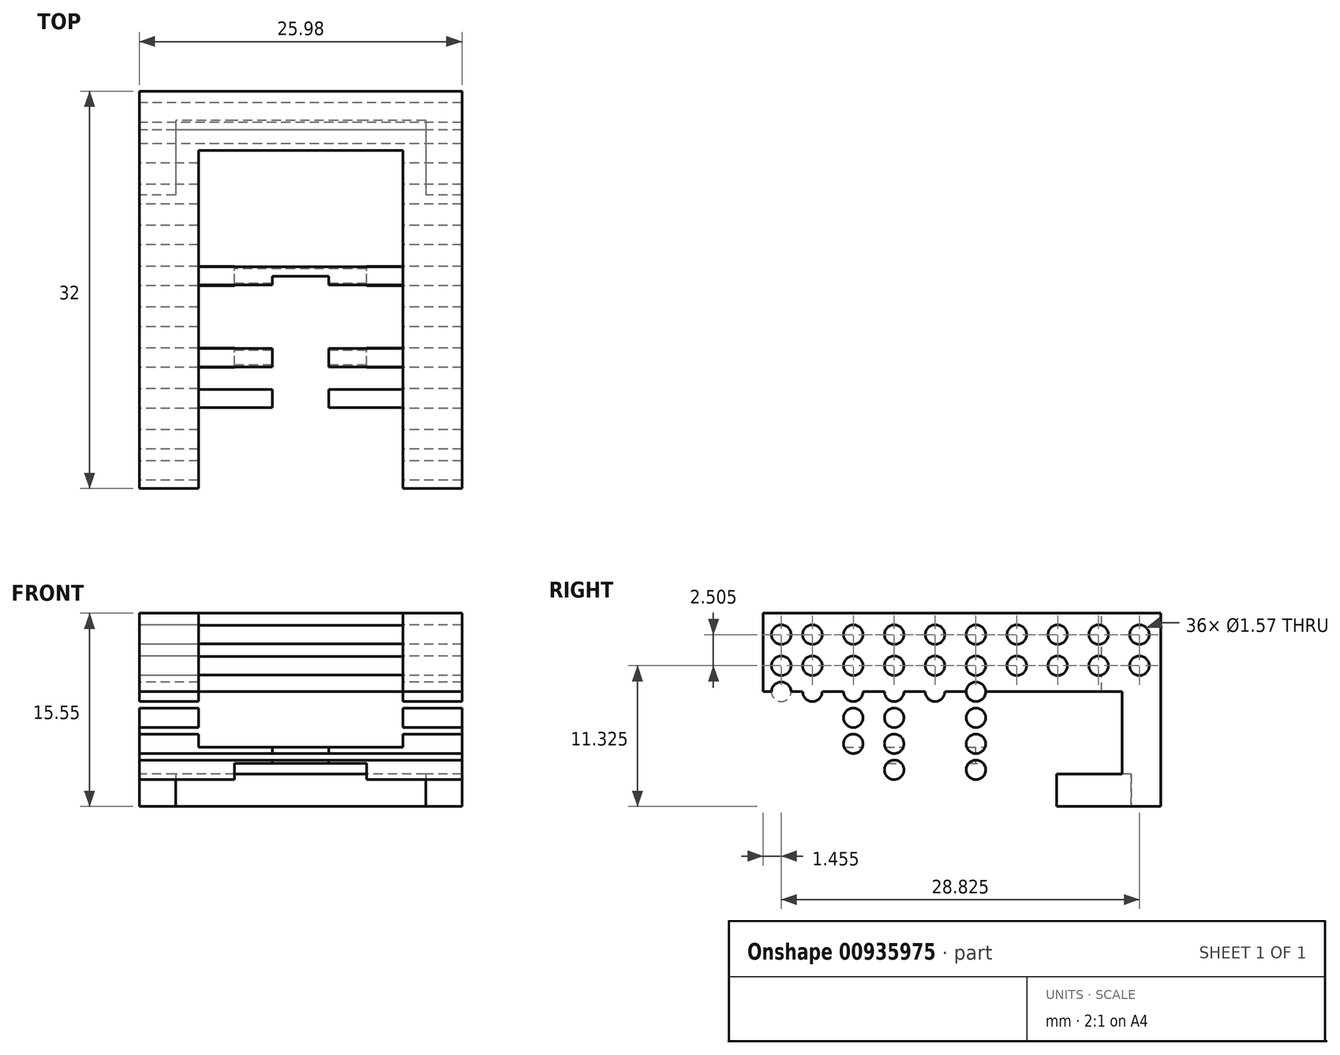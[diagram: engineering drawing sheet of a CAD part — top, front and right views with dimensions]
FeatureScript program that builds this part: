
annotation { "Feature Type Name" : "Feature", "Feature Type Description" : "" }
export const myFeature = defineFeature(function(context is Context, id is Id, definition is map)
    precondition{}
    {
        {
            var Q0;
            Q0=qCreatedBy(makeId("Front.planeOp"),FACE);
            var sketch = newSketch(context, id + "F0", { "sketchPlane" : qUnion([Q0])});
            skLineSegment(sketch, "E0.bottom", {"start": v(8.22, 0) * mm, "end": v(-8.23, 0) * mm});
            skLineSegment(sketch, "E0.top", {"start": v(8.23, 15.55) * mm, "end": v(-8.22, 15.55) * mm});
            skLineSegment(sketch, "E0.left", {"start": v(8.22, 0) * mm, "end": v(8.23, 15.55) * mm});
            skLineSegment(sketch, "E0.right", {"start": v(-8.23, 0) * mm, "end": v(-8.22, 15.55) * mm});
            skPoint(sketch, "E0.middle", {"position": v(0, 7.78) * mm});
            skLineSegment(sketch, "E1.bottom", {"start": v(8.23, 15.55) * mm, "end": v(12.99, 15.55) * mm});
            skLineSegment(sketch, "E1.top", {"start": v(8.23, 0) * mm, "end": v(12.98, 0) * mm});
            skLineSegment(sketch, "E1.left", {"start": v(8.23, 15.55) * mm, "end": v(8.23, 0) * mm});
            skLineSegment(sketch, "E1.right", {"start": v(12.99, 15.55) * mm, "end": v(12.98, 0) * mm});
            skLineSegment(sketch, "E2.bottom", {"start": v(-8.23, 0) * mm, "end": v(-12.98, 0) * mm});
            skLineSegment(sketch, "E2.top", {"start": v(-8.23, 15.55) * mm, "end": v(-12.98, 15.55) * mm});
            skLineSegment(sketch, "E2.left", {"start": v(-8.23, 0) * mm, "end": v(-8.23, 15.55) * mm});
            skLineSegment(sketch, "E2.right", {"start": v(-12.98, 0) * mm, "end": v(-12.98, 15.55) * mm});
            skSolve(sketch);
        }
        {
            var Q0;
            Q0=makeQuery(id+"F0.imprint","IMPRINT",FACE,{"disambiguationData":[TD([[makeQuery(id+"F0.imprint","IMPRINT",EDGE,{"derivedFrom":sQuery(id+"F0.wireOp",EDGE,"E2.bottom")}),-1.0]])]});
            var Q1;
            Q1=makeQuery(id+"F0.imprint","IMPRINT",FACE,{"disambiguationData":[TD([[makeQuery(id+"F0.imprint","IMPRINT",EDGE,{"derivedFrom":sQuery(id+"F0.wireOp",EDGE,"E1.bottom")}),-1.0]])]});
            extrude(context, id + "F1", {"entities" : qUnion([Q0, Q1]), "depth" : 32 * mm, "offsetDistance" : 25 * mm});
        }
        {
            var Q0;
            Q0=makeQuery(id+"F0.imprint","IMPRINT",FACE,{"disambiguationData":[TD([[makeQuery(id+"F0.imprint","IMPRINT",EDGE,{"derivedFrom":sQuery(id+"F0.wireOp",EDGE,"E0.bottom")}),-1.0]])]});
            extrude(context, id + "F2", {"entities" : qUnion([Q0]), "operationType" : NewBodyOperationType.ADD, "depth" : 4.76 * mm, "offsetDistance" : 25 * mm});
        }
        {
            var Q0;
            Q0=makeQuery(id+"F2.opExtrude","CAP_FACE",FACE,{"disambiguationData":[OSD([sQuery(id+"F0.wireOp",EDGE,"E0.bottom"),sQuery(id+"F0.wireOp",EDGE,"E0.top"),sQuery(id+"F0.wireOp",EDGE,"E1.left"),sQuery(id+"F0.wireOp",EDGE,"E2.left")])],"isStart":false});
            var sketch = newSketch(context, id + "F3", { "sketchPlane" : qUnion([Q0])});
            skLineSegment(sketch, "E3.bottom", {"start": v(-8.23, 0) * mm, "end": v(8.23, 0) * mm});
            skLineSegment(sketch, "E3.top", {"start": v(-8.23, 4.76) * mm, "end": v(8.23, 4.76) * mm});
            skLineSegment(sketch, "E3.left", {"start": v(-8.23, 0) * mm, "end": v(-8.23, 4.76) * mm});
            skLineSegment(sketch, "E3.right", {"start": v(8.23, 0) * mm, "end": v(8.23, 4.76) * mm});
            skLineSegment(sketch, "E4.bottom", {"start": v(-5.32, 3.46) * mm, "end": v(5.32, 3.46) * mm});
            skLineSegment(sketch, "E4.top", {"start": v(-5.32, 0) * mm, "end": v(5.32, 0) * mm});
            skLineSegment(sketch, "E4.left", {"start": v(-5.32, 3.46) * mm, "end": v(-5.32, 0) * mm});
            skLineSegment(sketch, "E4.right", {"start": v(5.32, 3.46) * mm, "end": v(5.32, 0) * mm});
            skSolve(sketch);
        }
        {
            var Q0;
            Q0=makeQuery(id+"F3.imprint","IMPRINT",FACE,{"disambiguationData":[TD([[makeQuery(id+"F3.imprint","IMPRINT",EDGE,{"derivedFrom":sQuery(id+"F3.wireOp",EDGE,"E3.top")}),-1.0]])]});
            extrude(context, id + "F4", {"entities" : qUnion([Q0]), "operationType" : NewBodyOperationType.ADD, "depth" : 27.24 * mm, "offsetDistance" : 25 * mm});
        }
        {
            var Q0;
            Q0=makeQuery(id+"F1.opExtrude","SWEPT_FACE",FACE,{"disambiguationData":[OSD([sQuery(id+"F0.wireOp",EDGE,"E2.right")])]});
            var sketch = newSketch(context, id + "F5", { "sketchPlane" : qUnion([Q0])});
            skLineSegment(sketch, "E5.bottom", {"start": v(0, 0) * mm, "end": v(4.76, 0) * mm});
            skLineSegment(sketch, "E5.top", {"start": v(0, -5) * mm, "end": v(4.76, -5) * mm});
            skLineSegment(sketch, "E5.left", {"start": v(0, 0) * mm, "end": v(0, -5) * mm});
            skLineSegment(sketch, "E5.right", {"start": v(4.76, 0) * mm, "end": v(4.76, -5) * mm});
            skLineSegment(sketch, "E6", {"start": v(0, 1.39) * mm, "end": v(8.37, 1.39) * mm});
            skLineSegment(sketch, "E7.bottom", {"start": v(8.37, 0) * mm, "end": v(12.6, 0) * mm});
            skLineSegment(sketch, "E7.top", {"start": v(8.37, 9.23) * mm, "end": v(12.6, 9.23) * mm});
            skLineSegment(sketch, "E7.left", {"start": v(8.37, 0) * mm, "end": v(8.37, 9.23) * mm});
            skLineSegment(sketch, "E7.right", {"start": v(12.6, 0) * mm, "end": v(12.6, 9.23) * mm});
            skLineSegment(sketch, "E8.bottom", {"start": v(8.37, 9.23) * mm, "end": v(3.12, 9.23) * mm});
            skLineSegment(sketch, "E8.top", {"start": v(8.37, 2.6) * mm, "end": v(3.12, 2.6) * mm});
            skLineSegment(sketch, "E8.left", {"start": v(8.37, 9.23) * mm, "end": v(8.37, 2.6) * mm});
            skLineSegment(sketch, "E8.right", {"start": v(3.12, 9.23) * mm, "end": v(3.12, 2.6) * mm});
            skLineSegment(sketch, "E9.bottom", {"start": v(-4.28, 0) * mm, "end": v(-0.52, 0) * mm});
            skLineSegment(sketch, "E9.top", {"start": v(-4.28, 2.6) * mm, "end": v(-0.52, 2.6) * mm});
            skLineSegment(sketch, "E9.left", {"start": v(-4.28, 0) * mm, "end": v(-4.28, 2.6) * mm});
            skLineSegment(sketch, "E9.right", {"start": v(-0.52, 0) * mm, "end": v(-0.52, 2.6) * mm});
            skSolve(sketch);
        }
        {
            var Q0;
            Q0=makeQuery(id+"F5.imprint","IMPRINT",FACE,{"disambiguationData":[TD([[makeQuery(id+"F5.imprint","IMPRINT",EDGE,{"derivedFrom":sQuery(id+"F5.wireOp",EDGE,"E8.bottom")}),1.0]])]});
            var Q1;
            {var subQ3=sQuery(id+"F5.wireOp",EDGE,"E7.bottom");Q1=makeQuery(id+"F5.imprint","IMPRINT",FACE,{"disambiguationData":[TD([[makeQuery(id+"F5.imprint","IMPRINT",EDGE,{"derivedFrom":subQ3}),-1.0]])]});}
            extrude(context, id + "F6", {"entities" : qUnion([Q0, Q1]), "operationType" : NewBodyOperationType.REMOVE, "oppositeDirection" : true, "depth" : 25.98 * mm, "offsetDistance" : 25 * mm});
        }
        {
            var Q0;
            Q0=makeQuery(id+"F4.opExtrude","SWEPT_FACE",FACE,{"disambiguationData":[OSD([sQuery(id+"F3.wireOp",EDGE,"E3.top")])]});
            var sketch = newSketch(context, id + "F7", { "sketchPlane" : qUnion([Q0])});
            skLineSegment(sketch, "E10.bottom", {"start": v(2.27, -29.7) * mm, "end": v(-2.28, -29.7) * mm});
            skLineSegment(sketch, "E10.top", {"start": v(2.28, -14.9) * mm, "end": v(-2.27, -14.9) * mm});
            skLineSegment(sketch, "E10.left", {"start": v(2.27, -29.7) * mm, "end": v(2.28, -14.9) * mm});
            skLineSegment(sketch, "E10.right", {"start": v(-2.28, -29.7) * mm, "end": v(-2.27, -14.9) * mm});
            skPoint(sketch, "E10.middle", {"position": v(0, -22.3) * mm});
            skPoint(sketch, "E10.middle.positionSnap0", {"position": v(0, -32) * mm});
            skPoint(sketch, "E10.middle.positionSnap1", {"position": v(-8.23, -22.3) * mm});
            skPoint(sketch, "E10.centerSnap0", {"position": v(0, -32) * mm});
            skPoint(sketch, "E10.centerSnap1", {"position": v(-8.23, -22.3) * mm});
            skSolve(sketch);
        }
        {
            var Q0;
            Q0=makeQuery(id+"F7.imprint","IMPRINT",FACE,{"disambiguationData":[TD([[makeQuery(id+"F7.imprint","IMPRINT",EDGE,{"derivedFrom":sQuery(id+"F7.wireOp",EDGE,"E10.bottom")}),-1.0]])]});
            extrude(context, id + "F8", {"entities" : qUnion([Q0]), "operationType" : NewBodyOperationType.REMOVE, "oppositeDirection" : true, "depth" : 2 * mm, "offsetDistance" : 25 * mm});
        }
        {
            var Q0;
            Q0=makeQuery(id+"F1.opExtrude","SWEPT_FACE",FACE,{"disambiguationData":[OSD([sQuery(id+"F0.wireOp",EDGE,"E2.right")])]});
            var sketch = newSketch(context, id + "F9", { "sketchPlane" : qUnion([Q0])});
            skLineSegment(sketch, "E11.bottom", {"start": v(32, 15.55) * mm, "end": v(0, 15.55) * mm});
            skLineSegment(sketch, "E11.top", {"start": v(32, 9.23) * mm, "end": v(0, 9.23) * mm});
            skLineSegment(sketch, "E11.left", {"start": v(32, 15.55) * mm, "end": v(32, 9.23) * mm});
            skLineSegment(sketch, "E11.right", {"start": v(0, 15.55) * mm, "end": v(0, 9.23) * mm});
            skLineSegment(sketch, "E12.bottom", {"start": v(32, 0) * mm, "end": v(37.47, 0) * mm});
            skLineSegment(sketch, "E12.top", {"start": v(32, 4.76) * mm, "end": v(37.47, 4.76) * mm});
            skLineSegment(sketch, "E12.left", {"start": v(32, 0) * mm, "end": v(32, 4.76) * mm});
            skLineSegment(sketch, "E12.right", {"start": v(37.47, 0) * mm, "end": v(37.47, 4.76) * mm});
            skLineSegment(sketch, "E13.bottom", {"start": v(12.6, 9.23) * mm, "end": v(32, 9.23) * mm});
            skLineSegment(sketch, "E13.left", {"start": v(12.6, 9.23) * mm, "end": v(12.6, 4.76) * mm});
            skLineSegment(sketch, "E13.right", {"start": v(32, 9.23) * mm, "end": v(32, 4.76) * mm});
            skLineSegment(sketch, "E14.bottom", {"start": v(-1.17, 15.55) * mm, "end": v(32.9, 15.55) * mm});
            skLineSegment(sketch, "E14.top", {"start": v(-1.17, 13.83) * mm, "end": v(32.9, 13.83) * mm});
            skLineSegment(sketch, "E14.left", {"start": v(-1.17, 15.55) * mm, "end": v(-1.17, 13.83) * mm});
            skLineSegment(sketch, "E14.right", {"start": v(32.9, 15.55) * mm, "end": v(32.9, 13.83) * mm});
            skLineSegment(sketch, "E15.bottom", {"start": v(0, 9.23) * mm, "end": v(1.72, 9.23) * mm});
            skLineSegment(sketch, "E15.top", {"start": v(0, 16.76) * mm, "end": v(1.72, 16.76) * mm});
            skLineSegment(sketch, "E15.left", {"start": v(0, 9.23) * mm, "end": v(0, 16.76) * mm});
            skLineSegment(sketch, "E15.right", {"start": v(1.72, 9.23) * mm, "end": v(1.72, 16.76) * mm});
            skCircle(sketch, "E16", {"center": v(1.72, 13.83) * mm, "radius": 0.79 * mm});
            skLineSegment(sketch, "E17.bottom", {"start": v(2.5, 9.23) * mm, "end": v(4.22, 9.23) * mm});
            skLineSegment(sketch, "E17.top", {"start": v(2.5, 16.72) * mm, "end": v(4.22, 16.72) * mm});
            skLineSegment(sketch, "E17.left", {"start": v(2.5, 9.23) * mm, "end": v(2.5, 16.72) * mm});
            skLineSegment(sketch, "E17.right", {"start": v(4.22, 9.23) * mm, "end": v(4.22, 16.72) * mm});
            skCircle(sketch, "E18", {"center": v(5, 13.83) * mm, "radius": 0.79 * mm});
            skLineSegment(sketch, "E19.bottom", {"start": v(5.8, 9.23) * mm, "end": v(7.51, 9.23) * mm});
            skLineSegment(sketch, "E19.top", {"start": v(5.8, 16.72) * mm, "end": v(7.51, 16.72) * mm});
            skLineSegment(sketch, "E19.left", {"start": v(5.8, 9.23) * mm, "end": v(5.8, 16.72) * mm});
            skLineSegment(sketch, "E19.right", {"start": v(7.51, 9.23) * mm, "end": v(7.51, 16.72) * mm});
            skCircle(sketch, "E20", {"center": v(8.3, 13.83) * mm, "radius": 0.79 * mm});
            skLineSegment(sketch, "E21.bottom", {"start": v(9.08, 9.23) * mm, "end": v(10.8, 9.23) * mm});
            skLineSegment(sketch, "E21.top", {"start": v(9.08, 16.72) * mm, "end": v(10.8, 16.72) * mm});
            skLineSegment(sketch, "E21.left", {"start": v(9.08, 9.23) * mm, "end": v(9.08, 16.72) * mm});
            skLineSegment(sketch, "E21.right", {"start": v(10.8, 9.23) * mm, "end": v(10.8, 16.72) * mm});
            skCircle(sketch, "E22", {"center": v(11.59, 13.83) * mm, "radius": 0.79 * mm});
            skLineSegment(sketch, "E23.bottom", {"start": v(12.37, 9.23) * mm, "end": v(14.1, 9.23) * mm});
            skLineSegment(sketch, "E23.top", {"start": v(12.37, 16.72) * mm, "end": v(14.1, 16.72) * mm});
            skLineSegment(sketch, "E23.left", {"start": v(12.37, 9.23) * mm, "end": v(12.37, 16.72) * mm});
            skLineSegment(sketch, "E23.right", {"start": v(14.1, 9.23) * mm, "end": v(14.1, 16.72) * mm});
            skCircle(sketch, "E24", {"center": v(14.88, 13.83) * mm, "radius": 0.79 * mm});
            skLineSegment(sketch, "E25.bottom", {"start": v(15.66, 9.23) * mm, "end": v(17.38, 9.23) * mm});
            skLineSegment(sketch, "E25.top", {"start": v(15.66, 16.72) * mm, "end": v(17.38, 16.72) * mm});
            skLineSegment(sketch, "E25.left", {"start": v(15.66, 9.23) * mm, "end": v(15.66, 16.72) * mm});
            skLineSegment(sketch, "E25.right", {"start": v(17.38, 9.23) * mm, "end": v(17.38, 16.72) * mm});
            skCircle(sketch, "E26", {"center": v(18.17, 13.83) * mm, "radius": 0.79 * mm});
            skLineSegment(sketch, "E27.bottom", {"start": v(18.95, 9.23) * mm, "end": v(20.67, 9.23) * mm});
            skLineSegment(sketch, "E27.top", {"start": v(18.95, 16.72) * mm, "end": v(20.67, 16.72) * mm});
            skLineSegment(sketch, "E27.left", {"start": v(18.95, 9.23) * mm, "end": v(18.95, 16.72) * mm});
            skLineSegment(sketch, "E27.right", {"start": v(20.67, 9.23) * mm, "end": v(20.67, 16.72) * mm});
            skCircle(sketch, "E28", {"center": v(21.46, 13.83) * mm, "radius": 0.79 * mm});
            skLineSegment(sketch, "E29.bottom", {"start": v(22.24, 9.23) * mm, "end": v(23.96, 9.23) * mm});
            skLineSegment(sketch, "E29.top", {"start": v(22.24, 16.72) * mm, "end": v(23.96, 16.72) * mm});
            skLineSegment(sketch, "E29.left", {"start": v(22.24, 9.23) * mm, "end": v(22.24, 16.72) * mm});
            skLineSegment(sketch, "E29.right", {"start": v(23.96, 9.23) * mm, "end": v(23.96, 16.72) * mm});
            skCircle(sketch, "E30", {"center": v(24.75, 13.83) * mm, "radius": 0.79 * mm});
            skLineSegment(sketch, "E31.bottom", {"start": v(25.53, 9.23) * mm, "end": v(27.25, 9.23) * mm});
            skLineSegment(sketch, "E31.top", {"start": v(25.53, 16.72) * mm, "end": v(27.25, 16.72) * mm});
            skLineSegment(sketch, "E31.left", {"start": v(25.53, 9.23) * mm, "end": v(25.53, 16.72) * mm});
            skLineSegment(sketch, "E31.right", {"start": v(27.25, 9.23) * mm, "end": v(27.25, 16.72) * mm});
            skCircle(sketch, "E32", {"center": v(28.04, 13.83) * mm, "radius": 0.79 * mm});
            skLineSegment(sketch, "E33.bottom", {"start": v(28.82, 9.23) * mm, "end": v(30.54, 9.23) * mm});
            skLineSegment(sketch, "E33.top", {"start": v(28.82, 16.72) * mm, "end": v(30.54, 16.72) * mm});
            skLineSegment(sketch, "E33.left", {"start": v(28.82, 9.23) * mm, "end": v(28.82, 16.72) * mm});
            skLineSegment(sketch, "E33.right", {"start": v(30.54, 9.23) * mm, "end": v(30.54, 16.72) * mm});
            skLineSegment(sketch, "E34.bottom", {"start": v(-1.17, 13.04) * mm, "end": v(32.9, 13.04) * mm});
            skLineSegment(sketch, "E34.top", {"start": v(-1.17, 11.32) * mm, "end": v(32.9, 11.32) * mm});
            skLineSegment(sketch, "E34.left", {"start": v(-1.17, 13.04) * mm, "end": v(-1.17, 11.32) * mm});
            skLineSegment(sketch, "E34.right", {"start": v(32.9, 13.04) * mm, "end": v(32.9, 11.32) * mm});
            skCircle(sketch, "E35", {"center": v(1.72, 11.32) * mm, "radius": 0.79 * mm});
            skCircle(sketch, "E36", {"center": v(5, 11.32) * mm, "radius": 0.79 * mm});
            skCircle(sketch, "E37", {"center": v(8.3, 11.32) * mm, "radius": 0.79 * mm});
            skCircle(sketch, "E38", {"center": v(11.59, 11.32) * mm, "radius": 0.79 * mm});
            skCircle(sketch, "E39", {"center": v(14.88, 11.32) * mm, "radius": 0.79 * mm});
            skCircle(sketch, "E40", {"center": v(18.17, 11.32) * mm, "radius": 0.79 * mm});
            skCircle(sketch, "E41", {"center": v(21.46, 11.32) * mm, "radius": 0.79 * mm});
            skCircle(sketch, "E42", {"center": v(24.75, 11.32) * mm, "radius": 0.79 * mm});
            skCircle(sketch, "E43", {"center": v(28.04, 11.32) * mm, "radius": 0.79 * mm});
            skCircle(sketch, "E44", {"center": v(30.54, 13.83) * mm, "radius": 0.79 * mm});
            skCircle(sketch, "E45", {"center": v(30.54, 11.32) * mm, "radius": 0.79 * mm});
            skPoint(sketch, "E46.firstSnap0", {"position": v(12.6, 7.13) * mm});
            skLineSegment(sketch, "E46.bottom", {"start": v(11.82, 7.13) * mm, "end": v(32.9, 7.13) * mm});
            skLineSegment(sketch, "E46.top", {"start": v(11.82, 5.04) * mm, "end": v(32.9, 5.04) * mm});
            skLineSegment(sketch, "E46.left", {"start": v(11.82, 7.13) * mm, "end": v(11.82, 5.04) * mm});
            skLineSegment(sketch, "E46.right", {"start": v(32.9, 7.13) * mm, "end": v(32.9, 5.04) * mm});
            skCircle(sketch, "E47", {"center": v(14.88, 7.13) * mm, "radius": 0.79 * mm});
            skCircle(sketch, "E48", {"center": v(18.17, 7.13) * mm, "radius": 0.79 * mm});
            skCircle(sketch, "E49", {"center": v(21.46, 7.13) * mm, "radius": 0.79 * mm});
            skCircle(sketch, "E50", {"center": v(24.75, 7.13) * mm, "radius": 0.79 * mm});
            skCircle(sketch, "E51", {"center": v(28.04, 7.13) * mm, "radius": 0.79 * mm});
            skCircle(sketch, "E52", {"center": v(30.54, 7.13) * mm, "radius": 0.79 * mm});
            skCircle(sketch, "E53", {"center": v(14.88, 9.23) * mm, "radius": 0.79 * mm});
            skCircle(sketch, "E54", {"center": v(18.17, 9.23) * mm, "radius": 0.79 * mm});
            skCircle(sketch, "E55", {"center": v(21.46, 9.23) * mm, "radius": 0.79 * mm});
            skCircle(sketch, "E56", {"center": v(24.75, 9.23) * mm, "radius": 0.79 * mm});
            skCircle(sketch, "E57", {"center": v(28.04, 9.23) * mm, "radius": 0.79 * mm});
            skCircle(sketch, "E58", {"center": v(30.54, 9.23) * mm, "radius": 0.79 * mm});
            skLineSegment(sketch, "E59", {"start": v(41.5, -2.03) * mm, "end": v(41.5, -4.13) * mm});
            skLineSegment(sketch, "E60.bottom", {"start": v(11.82, -2.6) * mm, "end": v(32.9, -2.6) * mm});
            skLineSegment(sketch, "E60.top", {"start": v(11.82, -4.69) * mm, "end": v(32.9, -4.69) * mm});
            skLineSegment(sketch, "E60.left", {"start": v(11.82, -2.6) * mm, "end": v(11.82, -4.69) * mm});
            skLineSegment(sketch, "E60.right", {"start": v(32.9, -2.6) * mm, "end": v(32.9, -4.69) * mm});
            skLineSegment(sketch, "E61.top", {"start": v(11.82, 2.94) * mm, "end": v(32.9, 2.94) * mm});
            skLineSegment(sketch, "E61.left", {"start": v(11.82, 5.04) * mm, "end": v(11.82, 2.94) * mm});
            skLineSegment(sketch, "E61.right", {"start": v(32.9, 5.04) * mm, "end": v(32.9, 2.94) * mm});
            skCircle(sketch, "E62", {"center": v(14.88, 5.04) * mm, "radius": 0.79 * mm});
            skCircle(sketch, "E63", {"center": v(18.17, 5.04) * mm, "radius": 0.79 * mm});
            skCircle(sketch, "E64", {"center": v(21.46, 5.04) * mm, "radius": 0.79 * mm});
            skCircle(sketch, "E65", {"center": v(24.75, 5.04) * mm, "radius": 0.79 * mm});
            skCircle(sketch, "E66", {"center": v(28.04, 5.04) * mm, "radius": 0.79 * mm});
            skCircle(sketch, "E67", {"center": v(30.54, 5.04) * mm, "radius": 0.79 * mm});
            skCircle(sketch, "E68", {"center": v(14.88, 2.94) * mm, "radius": 0.79 * mm});
            skCircle(sketch, "E69", {"center": v(18.17, 2.94) * mm, "radius": 0.79 * mm});
            skCircle(sketch, "E70", {"center": v(21.46, 2.94) * mm, "radius": 0.79 * mm});
            skCircle(sketch, "E71", {"center": v(24.75, 2.94) * mm, "radius": 0.79 * mm});
            skCircle(sketch, "E72", {"center": v(28.04, 2.94) * mm, "radius": 0.79 * mm});
            skCircle(sketch, "E73", {"center": v(30.54, 2.94) * mm, "radius": 0.79 * mm});
            skSolve(sketch);
        }
        {
            var Q0;
            {var subQ0=sQuery(id+"F9.wireOp",EDGE,"E16");var subQ1=sQuery(id+"F9.wireOp",EDGE,"E14.top");var subQ2=makeQuery(id+"F9.imprint","INTERSECT",VERTEX,{"derivedFrom":[subQ1,subQ0]});Q0=makeQuery(id+"F9.imprint","IMPRINT",FACE,{"disambiguationData":[TD([[makeQuery(id+"F9.imprint","IMPRINT",EDGE,{"disambiguationData":[TD([[subQ2,-1.0]])],"derivedFrom":subQ1}),-1.0]])]});}
            var Q1;
            {var subQ0=sQuery(id+"F9.wireOp",EDGE,"E16");var subQ1=sQuery(id+"F9.wireOp",EDGE,"E14.top");var subQ2=makeQuery(id+"F9.imprint","INTERSECT",VERTEX,{"derivedFrom":[subQ1,subQ0]});Q1=makeQuery(id+"F9.imprint","IMPRINT",FACE,{"disambiguationData":[TD([[makeQuery(id+"F9.imprint","IMPRINT",EDGE,{"disambiguationData":[TD([[subQ2,-1.0]])],"derivedFrom":subQ1}),1.0]])]});}
            var Q2;
            {var subQ0=sQuery(id+"F9.wireOp",EDGE,"E15.right");var subQ1=sQuery(id+"F9.wireOp",EDGE,"E14.top");var subQ2=makeQuery(id+"F9.imprint","INTERSECT",VERTEX,{"derivedFrom":[subQ1,subQ0]});Q2=makeQuery(id+"F9.imprint","IMPRINT",FACE,{"disambiguationData":[TD([[makeQuery(id+"F9.imprint","IMPRINT",EDGE,{"disambiguationData":[TD([[subQ2,-1.0]])],"derivedFrom":subQ0}),-1.0]])]});}
            var Q3;
            {var subQ0=sQuery(id+"F9.wireOp",EDGE,"E15.right");var subQ1=sQuery(id+"F9.wireOp",EDGE,"E14.top");var subQ2=makeQuery(id+"F9.imprint","INTERSECT",VERTEX,{"derivedFrom":[subQ1,subQ0]});Q3=makeQuery(id+"F9.imprint","IMPRINT",FACE,{"disambiguationData":[TD([[makeQuery(id+"F9.imprint","IMPRINT",EDGE,{"disambiguationData":[TD([[subQ2,-1.0]])],"derivedFrom":subQ1}),-1.0]])]});}
            var Q4;
            {var subQ0=sQuery(id+"F9.wireOp",EDGE,"E18");var subQ4=makeQuery(id+"F9.imprint","INTERSECT",VERTEX,{"derivedFrom":[subQ0,sQuery(id+"F9.wireOp",EDGE,"E34.bottom")]});Q4=makeQuery(id+"F9.imprint","IMPRINT",FACE,{"disambiguationData":[TD([[makeQuery(id+"F9.imprint","IMPRINT",EDGE,{"disambiguationData":[TD([[subQ4,1.0]])],"derivedFrom":subQ0}),1.0]])]});}
            var Q5;
            {var subQ0=sQuery(id+"F9.wireOp",EDGE,"E18");var subQ1=sQuery(id+"F9.wireOp",EDGE,"E14.top");var subQ2=makeQuery(id+"F9.imprint","INTERSECT",VERTEX,{"derivedFrom":[subQ1,sQuery(id+"F9.wireOp",EDGE,"E17.right"),subQ0]});Q5=makeQuery(id+"F9.imprint","IMPRINT",FACE,{"disambiguationData":[TD([[makeQuery(id+"F9.imprint","IMPRINT",EDGE,{"disambiguationData":[TD([[subQ2,-1.0]])],"derivedFrom":subQ1}),1.0]])]});}
            var Q6;
            {var subQ0=sQuery(id+"F9.wireOp",EDGE,"E20");var subQ4=makeQuery(id+"F9.imprint","INTERSECT",VERTEX,{"derivedFrom":[subQ0,sQuery(id+"F9.wireOp",EDGE,"E34.bottom")]});Q6=makeQuery(id+"F9.imprint","IMPRINT",FACE,{"disambiguationData":[TD([[makeQuery(id+"F9.imprint","IMPRINT",EDGE,{"disambiguationData":[TD([[subQ4,1.0]])],"derivedFrom":subQ0}),1.0]])]});}
            var Q7;
            {var subQ0=sQuery(id+"F9.wireOp",EDGE,"E20");var subQ1=sQuery(id+"F9.wireOp",EDGE,"E14.top");var subQ2=makeQuery(id+"F9.imprint","INTERSECT",VERTEX,{"derivedFrom":[subQ1,sQuery(id+"F9.wireOp",EDGE,"E19.right"),subQ0]});Q7=makeQuery(id+"F9.imprint","IMPRINT",FACE,{"disambiguationData":[TD([[makeQuery(id+"F9.imprint","IMPRINT",EDGE,{"disambiguationData":[TD([[subQ2,-1.0]])],"derivedFrom":subQ1}),1.0]])]});}
            var Q8;
            {var subQ0=sQuery(id+"F9.wireOp",EDGE,"E22");var subQ1=sQuery(id+"F9.wireOp",EDGE,"E14.top");var subQ2=makeQuery(id+"F9.imprint","INTERSECT",VERTEX,{"derivedFrom":[subQ1,sQuery(id+"F9.wireOp",EDGE,"E21.right"),subQ0]});Q8=makeQuery(id+"F9.imprint","IMPRINT",FACE,{"disambiguationData":[TD([[makeQuery(id+"F9.imprint","IMPRINT",EDGE,{"disambiguationData":[TD([[subQ2,-1.0]])],"derivedFrom":subQ1}),1.0]])]});}
            var Q9;
            {var subQ0=sQuery(id+"F9.wireOp",EDGE,"E22");var subQ4=makeQuery(id+"F9.imprint","INTERSECT",VERTEX,{"derivedFrom":[subQ0,sQuery(id+"F9.wireOp",EDGE,"E34.bottom")]});Q9=makeQuery(id+"F9.imprint","IMPRINT",FACE,{"disambiguationData":[TD([[makeQuery(id+"F9.imprint","IMPRINT",EDGE,{"disambiguationData":[TD([[subQ4,1.0]])],"derivedFrom":subQ0}),1.0]])]});}
            var Q10;
            {var subQ0=sQuery(id+"F9.wireOp",EDGE,"E24");var subQ4=makeQuery(id+"F9.imprint","INTERSECT",VERTEX,{"derivedFrom":[subQ0,sQuery(id+"F9.wireOp",EDGE,"E34.bottom")]});Q10=makeQuery(id+"F9.imprint","IMPRINT",FACE,{"disambiguationData":[TD([[makeQuery(id+"F9.imprint","IMPRINT",EDGE,{"disambiguationData":[TD([[subQ4,1.0]])],"derivedFrom":subQ0}),1.0]])]});}
            var Q11;
            {var subQ0=sQuery(id+"F9.wireOp",EDGE,"E24");var subQ1=sQuery(id+"F9.wireOp",EDGE,"E14.top");var subQ2=makeQuery(id+"F9.imprint","INTERSECT",VERTEX,{"derivedFrom":[subQ1,sQuery(id+"F9.wireOp",EDGE,"E23.right"),subQ0]});Q11=makeQuery(id+"F9.imprint","IMPRINT",FACE,{"disambiguationData":[TD([[makeQuery(id+"F9.imprint","IMPRINT",EDGE,{"disambiguationData":[TD([[subQ2,-1.0]])],"derivedFrom":subQ1}),1.0]])]});}
            var Q12;
            {var subQ0=sQuery(id+"F9.wireOp",EDGE,"E26");var subQ1=sQuery(id+"F9.wireOp",EDGE,"E14.top");var subQ2=makeQuery(id+"F9.imprint","INTERSECT",VERTEX,{"derivedFrom":[subQ1,sQuery(id+"F9.wireOp",EDGE,"E25.right"),subQ0]});Q12=makeQuery(id+"F9.imprint","IMPRINT",FACE,{"disambiguationData":[TD([[makeQuery(id+"F9.imprint","IMPRINT",EDGE,{"disambiguationData":[TD([[subQ2,-1.0]])],"derivedFrom":subQ1}),1.0]])]});}
            var Q13;
            {var subQ0=sQuery(id+"F9.wireOp",EDGE,"E26");var subQ4=makeQuery(id+"F9.imprint","INTERSECT",VERTEX,{"derivedFrom":[subQ0,sQuery(id+"F9.wireOp",EDGE,"E34.bottom")]});Q13=makeQuery(id+"F9.imprint","IMPRINT",FACE,{"disambiguationData":[TD([[makeQuery(id+"F9.imprint","IMPRINT",EDGE,{"disambiguationData":[TD([[subQ4,1.0]])],"derivedFrom":subQ0}),1.0]])]});}
            var Q14;
            {var subQ0=sQuery(id+"F9.wireOp",EDGE,"E28");var subQ4=makeQuery(id+"F9.imprint","INTERSECT",VERTEX,{"derivedFrom":[subQ0,sQuery(id+"F9.wireOp",EDGE,"E34.bottom")]});Q14=makeQuery(id+"F9.imprint","IMPRINT",FACE,{"disambiguationData":[TD([[makeQuery(id+"F9.imprint","IMPRINT",EDGE,{"disambiguationData":[TD([[subQ4,1.0]])],"derivedFrom":subQ0}),1.0]])]});}
            var Q15;
            {var subQ0=sQuery(id+"F9.wireOp",EDGE,"E28");var subQ1=sQuery(id+"F9.wireOp",EDGE,"E14.top");var subQ2=makeQuery(id+"F9.imprint","INTERSECT",VERTEX,{"derivedFrom":[subQ1,sQuery(id+"F9.wireOp",EDGE,"E27.right"),subQ0]});Q15=makeQuery(id+"F9.imprint","IMPRINT",FACE,{"disambiguationData":[TD([[makeQuery(id+"F9.imprint","IMPRINT",EDGE,{"disambiguationData":[TD([[subQ2,-1.0]])],"derivedFrom":subQ1}),1.0]])]});}
            var Q16;
            {var subQ0=sQuery(id+"F9.wireOp",EDGE,"E30");var subQ1=sQuery(id+"F9.wireOp",EDGE,"E14.top");var subQ2=makeQuery(id+"F9.imprint","INTERSECT",VERTEX,{"derivedFrom":[subQ1,sQuery(id+"F9.wireOp",EDGE,"E29.right"),subQ0]});Q16=makeQuery(id+"F9.imprint","IMPRINT",FACE,{"disambiguationData":[TD([[makeQuery(id+"F9.imprint","IMPRINT",EDGE,{"disambiguationData":[TD([[subQ2,-1.0]])],"derivedFrom":subQ1}),1.0]])]});}
            var Q17;
            {var subQ0=sQuery(id+"F9.wireOp",EDGE,"E30");var subQ4=makeQuery(id+"F9.imprint","INTERSECT",VERTEX,{"derivedFrom":[subQ0,sQuery(id+"F9.wireOp",EDGE,"E34.bottom")]});Q17=makeQuery(id+"F9.imprint","IMPRINT",FACE,{"disambiguationData":[TD([[makeQuery(id+"F9.imprint","IMPRINT",EDGE,{"disambiguationData":[TD([[subQ4,1.0]])],"derivedFrom":subQ0}),1.0]])]});}
            var Q18;
            {var subQ0=sQuery(id+"F9.wireOp",EDGE,"E32");var subQ1=sQuery(id+"F9.wireOp",EDGE,"E14.top");var subQ2=makeQuery(id+"F9.imprint","INTERSECT",VERTEX,{"derivedFrom":[subQ1,sQuery(id+"F9.wireOp",EDGE,"E31.right"),subQ0]});Q18=makeQuery(id+"F9.imprint","IMPRINT",FACE,{"disambiguationData":[TD([[makeQuery(id+"F9.imprint","IMPRINT",EDGE,{"disambiguationData":[TD([[subQ2,-1.0]])],"derivedFrom":subQ1}),1.0]])]});}
            var Q19;
            {var subQ0=sQuery(id+"F9.wireOp",EDGE,"E32");var subQ4=makeQuery(id+"F9.imprint","INTERSECT",VERTEX,{"derivedFrom":[subQ0,sQuery(id+"F9.wireOp",EDGE,"E34.bottom")]});Q19=makeQuery(id+"F9.imprint","IMPRINT",FACE,{"disambiguationData":[TD([[makeQuery(id+"F9.imprint","IMPRINT",EDGE,{"disambiguationData":[TD([[subQ4,1.0]])],"derivedFrom":subQ0}),1.0]])]});}
            var Q20;
            {var subQ0=sQuery(id+"F9.wireOp",EDGE,"E44");var subQ1=sQuery(id+"F9.wireOp",EDGE,"E14.top");var subQ2=makeQuery(id+"F9.imprint","INTERSECT",VERTEX,{"disambiguationData":[OD(0.0)],"derivedFrom":[subQ1,subQ0]});Q20=makeQuery(id+"F9.imprint","IMPRINT",FACE,{"disambiguationData":[TD([[makeQuery(id+"F9.imprint","IMPRINT",EDGE,{"disambiguationData":[TD([[subQ2,-1.0]])],"derivedFrom":subQ1}),1.0]])]});}
            var Q21;
            {var subQ0=sQuery(id+"F9.wireOp",EDGE,"E33.right");var subQ1=sQuery(id+"F9.wireOp",EDGE,"E14.top");var subQ2=makeQuery(id+"F9.imprint","INTERSECT",VERTEX,{"derivedFrom":[subQ1,subQ0]});Q21=makeQuery(id+"F9.imprint","IMPRINT",FACE,{"disambiguationData":[TD([[makeQuery(id+"F9.imprint","IMPRINT",EDGE,{"disambiguationData":[TD([[subQ2,-1.0]])],"derivedFrom":subQ1}),1.0]])]});}
            var Q22;
            {var subQ0=sQuery(id+"F9.wireOp",EDGE,"E44");var subQ1=sQuery(id+"F9.wireOp",EDGE,"E14.top");var subQ2=makeQuery(id+"F9.imprint","INTERSECT",VERTEX,{"disambiguationData":[OD(0.0)],"derivedFrom":[subQ1,subQ0]});Q22=makeQuery(id+"F9.imprint","IMPRINT",FACE,{"disambiguationData":[TD([[makeQuery(id+"F9.imprint","IMPRINT",EDGE,{"disambiguationData":[TD([[subQ2,-1.0]])],"derivedFrom":subQ1}),-1.0]])]});}
            var Q23;
            {var subQ0=sQuery(id+"F9.wireOp",EDGE,"E33.right");var subQ1=sQuery(id+"F9.wireOp",EDGE,"E14.top");var subQ2=makeQuery(id+"F9.imprint","INTERSECT",VERTEX,{"derivedFrom":[subQ1,subQ0]});Q23=makeQuery(id+"F9.imprint","IMPRINT",FACE,{"disambiguationData":[TD([[makeQuery(id+"F9.imprint","IMPRINT",EDGE,{"disambiguationData":[TD([[subQ2,-1.0]])],"derivedFrom":subQ1}),-1.0]])]});}
            var Q24;
            {var subQ0=sQuery(id+"F9.wireOp",EDGE,"E34.top");var subQ1=sQuery(id+"F9.wireOp",EDGE,"E33.right");var subQ2=makeQuery(id+"F9.imprint","INTERSECT",VERTEX,{"derivedFrom":[subQ1,subQ0]});Q24=makeQuery(id+"F9.imprint","IMPRINT",FACE,{"disambiguationData":[TD([[makeQuery(id+"F9.imprint","IMPRINT",EDGE,{"disambiguationData":[TD([[subQ2,-1.0]])],"derivedFrom":subQ1}),1.0]])]});}
            var Q25;
            {var subQ0=sQuery(id+"F9.wireOp",EDGE,"E34.top");var subQ1=sQuery(id+"F9.wireOp",EDGE,"E33.right");var subQ2=makeQuery(id+"F9.imprint","INTERSECT",VERTEX,{"derivedFrom":[subQ1,subQ0]});Q25=makeQuery(id+"F9.imprint","IMPRINT",FACE,{"disambiguationData":[TD([[makeQuery(id+"F9.imprint","IMPRINT",EDGE,{"disambiguationData":[TD([[subQ2,-1.0]])],"derivedFrom":subQ1}),-1.0]])]});}
            var Q26;
            {var subQ0=sQuery(id+"F9.wireOp",EDGE,"E45");var subQ1=sQuery(id+"F9.wireOp",EDGE,"E33.right");var subQ2=makeQuery(id+"F9.imprint","INTERSECT",VERTEX,{"disambiguationData":[OD(0.0)],"derivedFrom":[subQ1,subQ0]});Q26=makeQuery(id+"F9.imprint","IMPRINT",FACE,{"disambiguationData":[TD([[makeQuery(id+"F9.imprint","IMPRINT",EDGE,{"disambiguationData":[TD([[subQ2,-1.0]])],"derivedFrom":subQ1}),1.0]])]});}
            var Q27;
            {var subQ0=sQuery(id+"F9.wireOp",EDGE,"E45");var subQ1=sQuery(id+"F9.wireOp",EDGE,"E33.right");var subQ2=makeQuery(id+"F9.imprint","INTERSECT",VERTEX,{"disambiguationData":[OD(0.0)],"derivedFrom":[subQ1,subQ0]});Q27=makeQuery(id+"F9.imprint","IMPRINT",FACE,{"disambiguationData":[TD([[makeQuery(id+"F9.imprint","IMPRINT",EDGE,{"disambiguationData":[TD([[subQ2,-1.0]])],"derivedFrom":subQ1}),-1.0]])]});}
            var Q28;
            {var subQ0=sQuery(id+"F9.wireOp",EDGE,"E43");var subQ1=sQuery(id+"F9.wireOp",EDGE,"E34.top");var subQ2=makeQuery(id+"F9.imprint","INTERSECT",VERTEX,{"derivedFrom":[sQuery(id+"F9.wireOp",EDGE,"E31.right"),subQ1,subQ0]});Q28=makeQuery(id+"F9.imprint","IMPRINT",FACE,{"disambiguationData":[TD([[makeQuery(id+"F9.imprint","IMPRINT",EDGE,{"disambiguationData":[TD([[subQ2,-1.0]])],"derivedFrom":subQ1}),-1.0]])]});}
            var Q29;
            {var subQ0=sQuery(id+"F9.wireOp",EDGE,"E43");var subQ1=sQuery(id+"F9.wireOp",EDGE,"E34.top");var subQ2=makeQuery(id+"F9.imprint","INTERSECT",VERTEX,{"derivedFrom":[sQuery(id+"F9.wireOp",EDGE,"E31.right"),subQ1,subQ0]});Q29=makeQuery(id+"F9.imprint","IMPRINT",FACE,{"disambiguationData":[TD([[makeQuery(id+"F9.imprint","IMPRINT",EDGE,{"disambiguationData":[TD([[subQ2,-1.0]])],"derivedFrom":subQ1}),1.0]])]});}
            var Q30;
            {var subQ0=sQuery(id+"F9.wireOp",EDGE,"E42");var subQ1=sQuery(id+"F9.wireOp",EDGE,"E34.top");var subQ2=makeQuery(id+"F9.imprint","INTERSECT",VERTEX,{"derivedFrom":[sQuery(id+"F9.wireOp",EDGE,"E29.right"),subQ1,subQ0]});Q30=makeQuery(id+"F9.imprint","IMPRINT",FACE,{"disambiguationData":[TD([[makeQuery(id+"F9.imprint","IMPRINT",EDGE,{"disambiguationData":[TD([[subQ2,-1.0]])],"derivedFrom":subQ1}),-1.0]])]});}
            var Q31;
            {var subQ0=sQuery(id+"F9.wireOp",EDGE,"E42");var subQ1=sQuery(id+"F9.wireOp",EDGE,"E34.top");var subQ2=makeQuery(id+"F9.imprint","INTERSECT",VERTEX,{"derivedFrom":[sQuery(id+"F9.wireOp",EDGE,"E29.right"),subQ1,subQ0]});Q31=makeQuery(id+"F9.imprint","IMPRINT",FACE,{"disambiguationData":[TD([[makeQuery(id+"F9.imprint","IMPRINT",EDGE,{"disambiguationData":[TD([[subQ2,-1.0]])],"derivedFrom":subQ1}),1.0]])]});}
            var Q32;
            {var subQ0=sQuery(id+"F9.wireOp",EDGE,"E41");var subQ1=sQuery(id+"F9.wireOp",EDGE,"E34.top");var subQ2=makeQuery(id+"F9.imprint","INTERSECT",VERTEX,{"derivedFrom":[sQuery(id+"F9.wireOp",EDGE,"E27.right"),subQ1,subQ0]});Q32=makeQuery(id+"F9.imprint","IMPRINT",FACE,{"disambiguationData":[TD([[makeQuery(id+"F9.imprint","IMPRINT",EDGE,{"disambiguationData":[TD([[subQ2,-1.0]])],"derivedFrom":subQ1}),-1.0]])]});}
            var Q33;
            {var subQ0=sQuery(id+"F9.wireOp",EDGE,"E41");var subQ1=sQuery(id+"F9.wireOp",EDGE,"E34.top");var subQ2=makeQuery(id+"F9.imprint","INTERSECT",VERTEX,{"derivedFrom":[sQuery(id+"F9.wireOp",EDGE,"E27.right"),subQ1,subQ0]});Q33=makeQuery(id+"F9.imprint","IMPRINT",FACE,{"disambiguationData":[TD([[makeQuery(id+"F9.imprint","IMPRINT",EDGE,{"disambiguationData":[TD([[subQ2,-1.0]])],"derivedFrom":subQ1}),1.0]])]});}
            var Q34;
            {var subQ0=sQuery(id+"F9.wireOp",EDGE,"E40");var subQ1=sQuery(id+"F9.wireOp",EDGE,"E34.top");var subQ2=makeQuery(id+"F9.imprint","INTERSECT",VERTEX,{"derivedFrom":[sQuery(id+"F9.wireOp",EDGE,"E25.right"),subQ1,subQ0]});Q34=makeQuery(id+"F9.imprint","IMPRINT",FACE,{"disambiguationData":[TD([[makeQuery(id+"F9.imprint","IMPRINT",EDGE,{"disambiguationData":[TD([[subQ2,-1.0]])],"derivedFrom":subQ1}),-1.0]])]});}
            var Q35;
            {var subQ0=sQuery(id+"F9.wireOp",EDGE,"E40");var subQ1=sQuery(id+"F9.wireOp",EDGE,"E34.top");var subQ2=makeQuery(id+"F9.imprint","INTERSECT",VERTEX,{"derivedFrom":[sQuery(id+"F9.wireOp",EDGE,"E25.right"),subQ1,subQ0]});Q35=makeQuery(id+"F9.imprint","IMPRINT",FACE,{"disambiguationData":[TD([[makeQuery(id+"F9.imprint","IMPRINT",EDGE,{"disambiguationData":[TD([[subQ2,-1.0]])],"derivedFrom":subQ1}),1.0]])]});}
            var Q36;
            {var subQ0=sQuery(id+"F9.wireOp",EDGE,"E39");var subQ1=sQuery(id+"F9.wireOp",EDGE,"E34.top");var subQ2=makeQuery(id+"F9.imprint","INTERSECT",VERTEX,{"derivedFrom":[sQuery(id+"F9.wireOp",EDGE,"E23.right"),subQ1,subQ0]});Q36=makeQuery(id+"F9.imprint","IMPRINT",FACE,{"disambiguationData":[TD([[makeQuery(id+"F9.imprint","IMPRINT",EDGE,{"disambiguationData":[TD([[subQ2,-1.0]])],"derivedFrom":subQ1}),-1.0]])]});}
            var Q37;
            {var subQ0=sQuery(id+"F9.wireOp",EDGE,"E39");var subQ1=sQuery(id+"F9.wireOp",EDGE,"E34.top");var subQ2=makeQuery(id+"F9.imprint","INTERSECT",VERTEX,{"derivedFrom":[sQuery(id+"F9.wireOp",EDGE,"E23.right"),subQ1,subQ0]});Q37=makeQuery(id+"F9.imprint","IMPRINT",FACE,{"disambiguationData":[TD([[makeQuery(id+"F9.imprint","IMPRINT",EDGE,{"disambiguationData":[TD([[subQ2,-1.0]])],"derivedFrom":subQ1}),1.0]])]});}
            var Q38;
            {var subQ0=sQuery(id+"F9.wireOp",EDGE,"E38");var subQ1=sQuery(id+"F9.wireOp",EDGE,"E34.top");var subQ2=makeQuery(id+"F9.imprint","INTERSECT",VERTEX,{"derivedFrom":[sQuery(id+"F9.wireOp",EDGE,"E21.right"),subQ1,subQ0]});Q38=makeQuery(id+"F9.imprint","IMPRINT",FACE,{"disambiguationData":[TD([[makeQuery(id+"F9.imprint","IMPRINT",EDGE,{"disambiguationData":[TD([[subQ2,-1.0]])],"derivedFrom":subQ1}),-1.0]])]});}
            var Q39;
            {var subQ0=sQuery(id+"F9.wireOp",EDGE,"E38");var subQ1=sQuery(id+"F9.wireOp",EDGE,"E34.top");var subQ2=makeQuery(id+"F9.imprint","INTERSECT",VERTEX,{"derivedFrom":[sQuery(id+"F9.wireOp",EDGE,"E21.right"),subQ1,subQ0]});Q39=makeQuery(id+"F9.imprint","IMPRINT",FACE,{"disambiguationData":[TD([[makeQuery(id+"F9.imprint","IMPRINT",EDGE,{"disambiguationData":[TD([[subQ2,-1.0]])],"derivedFrom":subQ1}),1.0]])]});}
            var Q40;
            {var subQ0=sQuery(id+"F9.wireOp",EDGE,"E37");var subQ1=sQuery(id+"F9.wireOp",EDGE,"E34.top");var subQ2=makeQuery(id+"F9.imprint","INTERSECT",VERTEX,{"derivedFrom":[sQuery(id+"F9.wireOp",EDGE,"E19.right"),subQ1,subQ0]});Q40=makeQuery(id+"F9.imprint","IMPRINT",FACE,{"disambiguationData":[TD([[makeQuery(id+"F9.imprint","IMPRINT",EDGE,{"disambiguationData":[TD([[subQ2,-1.0]])],"derivedFrom":subQ1}),-1.0]])]});}
            var Q41;
            {var subQ0=sQuery(id+"F9.wireOp",EDGE,"E37");var subQ1=sQuery(id+"F9.wireOp",EDGE,"E34.top");var subQ2=makeQuery(id+"F9.imprint","INTERSECT",VERTEX,{"derivedFrom":[sQuery(id+"F9.wireOp",EDGE,"E19.right"),subQ1,subQ0]});Q41=makeQuery(id+"F9.imprint","IMPRINT",FACE,{"disambiguationData":[TD([[makeQuery(id+"F9.imprint","IMPRINT",EDGE,{"disambiguationData":[TD([[subQ2,-1.0]])],"derivedFrom":subQ1}),1.0]])]});}
            var Q42;
            {var subQ0=sQuery(id+"F9.wireOp",EDGE,"E36");var subQ1=sQuery(id+"F9.wireOp",EDGE,"E34.top");var subQ2=makeQuery(id+"F9.imprint","INTERSECT",VERTEX,{"derivedFrom":[sQuery(id+"F9.wireOp",EDGE,"E17.right"),subQ1,subQ0]});Q42=makeQuery(id+"F9.imprint","IMPRINT",FACE,{"disambiguationData":[TD([[makeQuery(id+"F9.imprint","IMPRINT",EDGE,{"disambiguationData":[TD([[subQ2,-1.0]])],"derivedFrom":subQ1}),-1.0]])]});}
            var Q43;
            {var subQ0=sQuery(id+"F9.wireOp",EDGE,"E36");var subQ1=sQuery(id+"F9.wireOp",EDGE,"E34.top");var subQ2=makeQuery(id+"F9.imprint","INTERSECT",VERTEX,{"derivedFrom":[sQuery(id+"F9.wireOp",EDGE,"E17.right"),subQ1,subQ0]});Q43=makeQuery(id+"F9.imprint","IMPRINT",FACE,{"disambiguationData":[TD([[makeQuery(id+"F9.imprint","IMPRINT",EDGE,{"disambiguationData":[TD([[subQ2,-1.0]])],"derivedFrom":subQ1}),1.0]])]});}
            var Q44;
            {var subQ0=sQuery(id+"F9.wireOp",EDGE,"E35");var subQ1=sQuery(id+"F9.wireOp",EDGE,"E15.right");var subQ2=makeQuery(id+"F9.imprint","INTERSECT",VERTEX,{"disambiguationData":[OD(0.0)],"derivedFrom":[subQ1,subQ0]});Q44=makeQuery(id+"F9.imprint","IMPRINT",FACE,{"disambiguationData":[TD([[makeQuery(id+"F9.imprint","IMPRINT",EDGE,{"disambiguationData":[TD([[subQ2,-1.0]])],"derivedFrom":subQ1}),-1.0]])]});}
            var Q45;
            {var subQ0=sQuery(id+"F9.wireOp",EDGE,"E35");var subQ1=sQuery(id+"F9.wireOp",EDGE,"E15.right");var subQ2=makeQuery(id+"F9.imprint","INTERSECT",VERTEX,{"disambiguationData":[OD(0.0)],"derivedFrom":[subQ1,subQ0]});Q45=makeQuery(id+"F9.imprint","IMPRINT",FACE,{"disambiguationData":[TD([[makeQuery(id+"F9.imprint","IMPRINT",EDGE,{"disambiguationData":[TD([[subQ2,-1.0]])],"derivedFrom":subQ1}),1.0]])]});}
            var Q46;
            {var subQ0=sQuery(id+"F9.wireOp",EDGE,"E34.top");var subQ1=sQuery(id+"F9.wireOp",EDGE,"E15.right");var subQ2=makeQuery(id+"F9.imprint","INTERSECT",VERTEX,{"derivedFrom":[subQ1,subQ0]});Q46=makeQuery(id+"F9.imprint","IMPRINT",FACE,{"disambiguationData":[TD([[makeQuery(id+"F9.imprint","IMPRINT",EDGE,{"disambiguationData":[TD([[subQ2,-1.0]])],"derivedFrom":subQ1}),1.0]])]});}
            var Q47;
            {var subQ0=sQuery(id+"F9.wireOp",EDGE,"E34.top");var subQ1=sQuery(id+"F9.wireOp",EDGE,"E15.right");var subQ2=makeQuery(id+"F9.imprint","INTERSECT",VERTEX,{"derivedFrom":[subQ1,subQ0]});Q47=makeQuery(id+"F9.imprint","IMPRINT",FACE,{"disambiguationData":[TD([[makeQuery(id+"F9.imprint","IMPRINT",EDGE,{"disambiguationData":[TD([[subQ2,-1.0]])],"derivedFrom":subQ1}),-1.0]])]});}
            var Q48;
            {var subQ0=sQuery(id+"F9.wireOp",EDGE,"E47");var subQ1=sQuery(id+"F9.wireOp",EDGE,"E46.bottom");var subQ2=makeQuery(id+"F9.imprint","INTERSECT",VERTEX,{"disambiguationData":[OD(0.0)],"derivedFrom":[subQ1,subQ0]});Q48=makeQuery(id+"F9.imprint","IMPRINT",FACE,{"disambiguationData":[TD([[makeQuery(id+"F9.imprint","IMPRINT",EDGE,{"disambiguationData":[TD([[subQ2,-1.0]])],"derivedFrom":subQ1}),1.0]])]});}
            var Q49;
            {var subQ0=sQuery(id+"F9.wireOp",EDGE,"E47");var subQ1=sQuery(id+"F9.wireOp",EDGE,"E46.bottom");var subQ2=makeQuery(id+"F9.imprint","INTERSECT",VERTEX,{"disambiguationData":[OD(0.0)],"derivedFrom":[subQ1,subQ0]});Q49=makeQuery(id+"F9.imprint","IMPRINT",FACE,{"disambiguationData":[TD([[makeQuery(id+"F9.imprint","IMPRINT",EDGE,{"disambiguationData":[TD([[subQ2,-1.0]])],"derivedFrom":subQ1}),-1.0]])]});}
            var Q50;
            {var subQ0=sQuery(id+"F9.wireOp",EDGE,"E48");var subQ1=sQuery(id+"F9.wireOp",EDGE,"E46.bottom");var subQ2=makeQuery(id+"F9.imprint","INTERSECT",VERTEX,{"disambiguationData":[OD(0.0)],"derivedFrom":[subQ1,subQ0]});Q50=makeQuery(id+"F9.imprint","IMPRINT",FACE,{"disambiguationData":[TD([[makeQuery(id+"F9.imprint","IMPRINT",EDGE,{"disambiguationData":[TD([[subQ2,-1.0]])],"derivedFrom":subQ1}),1.0]])]});}
            var Q51;
            {var subQ0=sQuery(id+"F9.wireOp",EDGE,"E48");var subQ1=sQuery(id+"F9.wireOp",EDGE,"E46.bottom");var subQ2=makeQuery(id+"F9.imprint","INTERSECT",VERTEX,{"disambiguationData":[OD(0.0)],"derivedFrom":[subQ1,subQ0]});Q51=makeQuery(id+"F9.imprint","IMPRINT",FACE,{"disambiguationData":[TD([[makeQuery(id+"F9.imprint","IMPRINT",EDGE,{"disambiguationData":[TD([[subQ2,-1.0]])],"derivedFrom":subQ1}),-1.0]])]});}
            var Q52;
            {var subQ0=sQuery(id+"F9.wireOp",EDGE,"E49");var subQ1=sQuery(id+"F9.wireOp",EDGE,"E46.bottom");var subQ2=makeQuery(id+"F9.imprint","INTERSECT",VERTEX,{"disambiguationData":[OD(0.0)],"derivedFrom":[subQ1,subQ0]});Q52=makeQuery(id+"F9.imprint","IMPRINT",FACE,{"disambiguationData":[TD([[makeQuery(id+"F9.imprint","IMPRINT",EDGE,{"disambiguationData":[TD([[subQ2,-1.0]])],"derivedFrom":subQ1}),1.0]])]});}
            var Q53;
            {var subQ0=sQuery(id+"F9.wireOp",EDGE,"E49");var subQ1=sQuery(id+"F9.wireOp",EDGE,"E46.bottom");var subQ2=makeQuery(id+"F9.imprint","INTERSECT",VERTEX,{"disambiguationData":[OD(0.0)],"derivedFrom":[subQ1,subQ0]});Q53=makeQuery(id+"F9.imprint","IMPRINT",FACE,{"disambiguationData":[TD([[makeQuery(id+"F9.imprint","IMPRINT",EDGE,{"disambiguationData":[TD([[subQ2,-1.0]])],"derivedFrom":subQ1}),-1.0]])]});}
            var Q54;
            {var subQ0=sQuery(id+"F9.wireOp",EDGE,"E50");var subQ1=sQuery(id+"F9.wireOp",EDGE,"E46.bottom");var subQ2=makeQuery(id+"F9.imprint","INTERSECT",VERTEX,{"disambiguationData":[OD(0.0)],"derivedFrom":[subQ1,subQ0]});Q54=makeQuery(id+"F9.imprint","IMPRINT",FACE,{"disambiguationData":[TD([[makeQuery(id+"F9.imprint","IMPRINT",EDGE,{"disambiguationData":[TD([[subQ2,-1.0]])],"derivedFrom":subQ1}),1.0]])]});}
            var Q55;
            {var subQ0=sQuery(id+"F9.wireOp",EDGE,"E50");var subQ1=sQuery(id+"F9.wireOp",EDGE,"E46.bottom");var subQ2=makeQuery(id+"F9.imprint","INTERSECT",VERTEX,{"disambiguationData":[OD(0.0)],"derivedFrom":[subQ1,subQ0]});Q55=makeQuery(id+"F9.imprint","IMPRINT",FACE,{"disambiguationData":[TD([[makeQuery(id+"F9.imprint","IMPRINT",EDGE,{"disambiguationData":[TD([[subQ2,-1.0]])],"derivedFrom":subQ1}),-1.0]])]});}
            var Q56;
            {var subQ0=sQuery(id+"F9.wireOp",EDGE,"E51");var subQ1=sQuery(id+"F9.wireOp",EDGE,"E46.bottom");var subQ2=makeQuery(id+"F9.imprint","INTERSECT",VERTEX,{"disambiguationData":[OD(0.0)],"derivedFrom":[subQ1,subQ0]});Q56=makeQuery(id+"F9.imprint","IMPRINT",FACE,{"disambiguationData":[TD([[makeQuery(id+"F9.imprint","IMPRINT",EDGE,{"disambiguationData":[TD([[subQ2,-1.0]])],"derivedFrom":subQ1}),1.0]])]});}
            var Q57;
            {var subQ0=sQuery(id+"F9.wireOp",EDGE,"E51");var subQ1=sQuery(id+"F9.wireOp",EDGE,"E46.bottom");var subQ2=makeQuery(id+"F9.imprint","INTERSECT",VERTEX,{"disambiguationData":[OD(0.0)],"derivedFrom":[subQ1,subQ0]});Q57=makeQuery(id+"F9.imprint","IMPRINT",FACE,{"disambiguationData":[TD([[makeQuery(id+"F9.imprint","IMPRINT",EDGE,{"disambiguationData":[TD([[subQ2,-1.0]])],"derivedFrom":subQ1}),-1.0]])]});}
            var Q58;
            {var subQ0=sQuery(id+"F9.wireOp",EDGE,"E52");var subQ1=sQuery(id+"F9.wireOp",EDGE,"E46.bottom");var subQ2=makeQuery(id+"F9.imprint","INTERSECT",VERTEX,{"disambiguationData":[OD(0.0)],"derivedFrom":[subQ1,subQ0]});Q58=makeQuery(id+"F9.imprint","IMPRINT",FACE,{"disambiguationData":[TD([[makeQuery(id+"F9.imprint","IMPRINT",EDGE,{"disambiguationData":[TD([[subQ2,-1.0]])],"derivedFrom":subQ1}),1.0]])]});}
            var Q59;
            {var subQ0=sQuery(id+"F9.wireOp",EDGE,"E52");var subQ1=sQuery(id+"F9.wireOp",EDGE,"E46.bottom");var subQ2=makeQuery(id+"F9.imprint","INTERSECT",VERTEX,{"disambiguationData":[OD(0.0)],"derivedFrom":[subQ1,subQ0]});Q59=makeQuery(id+"F9.imprint","IMPRINT",FACE,{"disambiguationData":[TD([[makeQuery(id+"F9.imprint","IMPRINT",EDGE,{"disambiguationData":[TD([[subQ2,-1.0]])],"derivedFrom":subQ1}),-1.0]])]});}
            var Q60;
            {var subQ0=sQuery(id+"F9.wireOp",EDGE,"E53");var subQ1=sQuery(id+"F9.wireOp",EDGE,"E13.bottom");var subQ2=makeQuery(id+"F9.imprint","INTERSECT",VERTEX,{"derivedFrom":[subQ1,sQuery(id+"F9.wireOp",EDGE,"E23.bottom"),sQuery(id+"F9.wireOp",EDGE,"E23.right"),subQ0]});Q60=makeQuery(id+"F9.imprint","IMPRINT",FACE,{"disambiguationData":[TD([[makeQuery(id+"F9.imprint","IMPRINT",EDGE,{"disambiguationData":[TD([[subQ2,-1.0]])],"derivedFrom":subQ1}),-1.0]])]});}
            var Q61;
            {var subQ0=sQuery(id+"F9.wireOp",EDGE,"E53");var subQ1=sQuery(id+"F9.wireOp",EDGE,"E13.bottom");var subQ2=makeQuery(id+"F9.imprint","INTERSECT",VERTEX,{"derivedFrom":[subQ1,sQuery(id+"F9.wireOp",EDGE,"E23.bottom"),sQuery(id+"F9.wireOp",EDGE,"E23.right"),subQ0]});Q61=makeQuery(id+"F9.imprint","IMPRINT",FACE,{"disambiguationData":[TD([[makeQuery(id+"F9.imprint","IMPRINT",EDGE,{"disambiguationData":[TD([[subQ2,-1.0]])],"derivedFrom":subQ1}),1.0]])]});}
            var Q62;
            {var subQ0=sQuery(id+"F9.wireOp",EDGE,"E54");var subQ1=sQuery(id+"F9.wireOp",EDGE,"E13.bottom");var subQ2=makeQuery(id+"F9.imprint","INTERSECT",VERTEX,{"derivedFrom":[subQ1,sQuery(id+"F9.wireOp",EDGE,"E25.bottom"),sQuery(id+"F9.wireOp",EDGE,"E25.right"),subQ0]});Q62=makeQuery(id+"F9.imprint","IMPRINT",FACE,{"disambiguationData":[TD([[makeQuery(id+"F9.imprint","IMPRINT",EDGE,{"disambiguationData":[TD([[subQ2,-1.0]])],"derivedFrom":subQ1}),1.0]])]});}
            var Q63;
            {var subQ0=sQuery(id+"F9.wireOp",EDGE,"E54");var subQ1=sQuery(id+"F9.wireOp",EDGE,"E13.bottom");var subQ2=makeQuery(id+"F9.imprint","INTERSECT",VERTEX,{"derivedFrom":[subQ1,sQuery(id+"F9.wireOp",EDGE,"E25.bottom"),sQuery(id+"F9.wireOp",EDGE,"E25.right"),subQ0]});Q63=makeQuery(id+"F9.imprint","IMPRINT",FACE,{"disambiguationData":[TD([[makeQuery(id+"F9.imprint","IMPRINT",EDGE,{"disambiguationData":[TD([[subQ2,-1.0]])],"derivedFrom":subQ1}),-1.0]])]});}
            var Q64;
            {var subQ0=sQuery(id+"F9.wireOp",EDGE,"E55");var subQ1=sQuery(id+"F9.wireOp",EDGE,"E13.bottom");var subQ2=makeQuery(id+"F9.imprint","INTERSECT",VERTEX,{"derivedFrom":[subQ1,sQuery(id+"F9.wireOp",EDGE,"E27.bottom"),sQuery(id+"F9.wireOp",EDGE,"E27.right"),subQ0]});Q64=makeQuery(id+"F9.imprint","IMPRINT",FACE,{"disambiguationData":[TD([[makeQuery(id+"F9.imprint","IMPRINT",EDGE,{"disambiguationData":[TD([[subQ2,-1.0]])],"derivedFrom":subQ1}),1.0]])]});}
            var Q65;
            {var subQ0=sQuery(id+"F9.wireOp",EDGE,"E55");var subQ1=sQuery(id+"F9.wireOp",EDGE,"E13.bottom");var subQ2=makeQuery(id+"F9.imprint","INTERSECT",VERTEX,{"derivedFrom":[subQ1,sQuery(id+"F9.wireOp",EDGE,"E27.bottom"),sQuery(id+"F9.wireOp",EDGE,"E27.right"),subQ0]});Q65=makeQuery(id+"F9.imprint","IMPRINT",FACE,{"disambiguationData":[TD([[makeQuery(id+"F9.imprint","IMPRINT",EDGE,{"disambiguationData":[TD([[subQ2,-1.0]])],"derivedFrom":subQ1}),-1.0]])]});}
            var Q66;
            {var subQ0=sQuery(id+"F9.wireOp",EDGE,"E56");var subQ1=sQuery(id+"F9.wireOp",EDGE,"E13.bottom");var subQ2=makeQuery(id+"F9.imprint","INTERSECT",VERTEX,{"derivedFrom":[subQ1,sQuery(id+"F9.wireOp",EDGE,"E29.bottom"),sQuery(id+"F9.wireOp",EDGE,"E29.right"),subQ0]});Q66=makeQuery(id+"F9.imprint","IMPRINT",FACE,{"disambiguationData":[TD([[makeQuery(id+"F9.imprint","IMPRINT",EDGE,{"disambiguationData":[TD([[subQ2,-1.0]])],"derivedFrom":subQ1}),1.0]])]});}
            var Q67;
            {var subQ0=sQuery(id+"F9.wireOp",EDGE,"E56");var subQ1=sQuery(id+"F9.wireOp",EDGE,"E13.bottom");var subQ2=makeQuery(id+"F9.imprint","INTERSECT",VERTEX,{"derivedFrom":[subQ1,sQuery(id+"F9.wireOp",EDGE,"E29.bottom"),sQuery(id+"F9.wireOp",EDGE,"E29.right"),subQ0]});Q67=makeQuery(id+"F9.imprint","IMPRINT",FACE,{"disambiguationData":[TD([[makeQuery(id+"F9.imprint","IMPRINT",EDGE,{"disambiguationData":[TD([[subQ2,-1.0]])],"derivedFrom":subQ1}),-1.0]])]});}
            var Q68;
            {var subQ0=sQuery(id+"F9.wireOp",EDGE,"E57");var subQ1=sQuery(id+"F9.wireOp",EDGE,"E13.bottom");var subQ2=makeQuery(id+"F9.imprint","INTERSECT",VERTEX,{"derivedFrom":[subQ1,sQuery(id+"F9.wireOp",EDGE,"E31.bottom"),sQuery(id+"F9.wireOp",EDGE,"E31.right"),subQ0]});Q68=makeQuery(id+"F9.imprint","IMPRINT",FACE,{"disambiguationData":[TD([[makeQuery(id+"F9.imprint","IMPRINT",EDGE,{"disambiguationData":[TD([[subQ2,-1.0]])],"derivedFrom":subQ1}),1.0]])]});}
            var Q69;
            {var subQ0=sQuery(id+"F9.wireOp",EDGE,"E57");var subQ1=sQuery(id+"F9.wireOp",EDGE,"E13.bottom");var subQ2=makeQuery(id+"F9.imprint","INTERSECT",VERTEX,{"derivedFrom":[subQ1,sQuery(id+"F9.wireOp",EDGE,"E31.bottom"),sQuery(id+"F9.wireOp",EDGE,"E31.right"),subQ0]});Q69=makeQuery(id+"F9.imprint","IMPRINT",FACE,{"disambiguationData":[TD([[makeQuery(id+"F9.imprint","IMPRINT",EDGE,{"disambiguationData":[TD([[subQ2,-1.0]])],"derivedFrom":subQ1}),-1.0]])]});}
            var Q70;
            {var subQ1=sQuery(id+"F9.wireOp",EDGE,"E13.bottom");var subQ3=sQuery(id+"F9.wireOp",EDGE,"E58");var subQ4=makeQuery(id+"F9.imprint","INTERSECT",VERTEX,{"derivedFrom":[subQ1,subQ3]});Q70=makeQuery(id+"F9.imprint","IMPRINT",FACE,{"disambiguationData":[TD([[makeQuery(id+"F9.imprint","IMPRINT",EDGE,{"disambiguationData":[TD([[subQ4,-1.0]])],"derivedFrom":subQ3}),1.0]])]});}
            var Q71;
            {var subQ1=sQuery(id+"F9.wireOp",EDGE,"E13.bottom");var subQ3=sQuery(id+"F9.wireOp",EDGE,"E58");var subQ4=makeQuery(id+"F9.imprint","INTERSECT",VERTEX,{"derivedFrom":[subQ1,subQ3]});Q71=makeQuery(id+"F9.imprint","IMPRINT",FACE,{"disambiguationData":[TD([[makeQuery(id+"F9.imprint","IMPRINT",EDGE,{"disambiguationData":[TD([[subQ4,1.0]])],"derivedFrom":subQ3}),1.0]])]});}
            var Q72;
            {var subQ1=sQuery(id+"F9.wireOp",EDGE,"E33.bottom");var subQ3=sQuery(id+"F9.wireOp",EDGE,"E58");var subQ4=makeQuery(id+"F9.imprint","INTERSECT",VERTEX,{"derivedFrom":[subQ1,subQ3]});Q72=makeQuery(id+"F9.imprint","IMPRINT",FACE,{"disambiguationData":[TD([[makeQuery(id+"F9.imprint","IMPRINT",EDGE,{"disambiguationData":[TD([[subQ4,1.0]])],"derivedFrom":subQ3}),1.0]])]});}
            var Q73;
            {var subQ0=sQuery(id+"F9.wireOp",EDGE,"E62");var subQ1=sQuery(id+"F9.wireOp",EDGE,"E46.top");var subQ2=makeQuery(id+"F9.imprint","INTERSECT",VERTEX,{"disambiguationData":[OD(0.0)],"derivedFrom":[subQ1,subQ0]});Q73=makeQuery(id+"F9.imprint","IMPRINT",FACE,{"disambiguationData":[TD([[makeQuery(id+"F9.imprint","IMPRINT",EDGE,{"disambiguationData":[TD([[subQ2,-1.0]])],"derivedFrom":subQ1}),1.0]])]});}
            var Q74;
            {var subQ0=sQuery(id+"F9.wireOp",EDGE,"E62");var subQ1=sQuery(id+"F9.wireOp",EDGE,"E46.top");var subQ2=makeQuery(id+"F9.imprint","INTERSECT",VERTEX,{"disambiguationData":[OD(0.0)],"derivedFrom":[subQ1,subQ0]});Q74=makeQuery(id+"F9.imprint","IMPRINT",FACE,{"disambiguationData":[TD([[makeQuery(id+"F9.imprint","IMPRINT",EDGE,{"disambiguationData":[TD([[subQ2,-1.0]])],"derivedFrom":subQ1}),-1.0]])]});}
            var Q75;
            {var subQ0=sQuery(id+"F9.wireOp",EDGE,"E63");var subQ1=sQuery(id+"F9.wireOp",EDGE,"E46.top");var subQ2=makeQuery(id+"F9.imprint","INTERSECT",VERTEX,{"disambiguationData":[OD(0.0)],"derivedFrom":[subQ1,subQ0]});Q75=makeQuery(id+"F9.imprint","IMPRINT",FACE,{"disambiguationData":[TD([[makeQuery(id+"F9.imprint","IMPRINT",EDGE,{"disambiguationData":[TD([[subQ2,-1.0]])],"derivedFrom":subQ1}),1.0]])]});}
            var Q76;
            {var subQ0=sQuery(id+"F9.wireOp",EDGE,"E63");var subQ1=sQuery(id+"F9.wireOp",EDGE,"E46.top");var subQ2=makeQuery(id+"F9.imprint","INTERSECT",VERTEX,{"disambiguationData":[OD(0.0)],"derivedFrom":[subQ1,subQ0]});Q76=makeQuery(id+"F9.imprint","IMPRINT",FACE,{"disambiguationData":[TD([[makeQuery(id+"F9.imprint","IMPRINT",EDGE,{"disambiguationData":[TD([[subQ2,-1.0]])],"derivedFrom":subQ1}),-1.0]])]});}
            var Q77;
            {var subQ0=sQuery(id+"F9.wireOp",EDGE,"E64");var subQ1=sQuery(id+"F9.wireOp",EDGE,"E46.top");var subQ2=makeQuery(id+"F9.imprint","INTERSECT",VERTEX,{"disambiguationData":[OD(0.0)],"derivedFrom":[subQ1,subQ0]});Q77=makeQuery(id+"F9.imprint","IMPRINT",FACE,{"disambiguationData":[TD([[makeQuery(id+"F9.imprint","IMPRINT",EDGE,{"disambiguationData":[TD([[subQ2,-1.0]])],"derivedFrom":subQ1}),1.0]])]});}
            var Q78;
            {var subQ0=sQuery(id+"F9.wireOp",EDGE,"E64");var subQ1=sQuery(id+"F9.wireOp",EDGE,"E46.top");var subQ2=makeQuery(id+"F9.imprint","INTERSECT",VERTEX,{"disambiguationData":[OD(0.0)],"derivedFrom":[subQ1,subQ0]});Q78=makeQuery(id+"F9.imprint","IMPRINT",FACE,{"disambiguationData":[TD([[makeQuery(id+"F9.imprint","IMPRINT",EDGE,{"disambiguationData":[TD([[subQ2,-1.0]])],"derivedFrom":subQ1}),-1.0]])]});}
            var Q79;
            {var subQ0=sQuery(id+"F9.wireOp",EDGE,"E65");var subQ1=sQuery(id+"F9.wireOp",EDGE,"E46.top");var subQ2=makeQuery(id+"F9.imprint","INTERSECT",VERTEX,{"disambiguationData":[OD(0.0)],"derivedFrom":[subQ1,subQ0]});Q79=makeQuery(id+"F9.imprint","IMPRINT",FACE,{"disambiguationData":[TD([[makeQuery(id+"F9.imprint","IMPRINT",EDGE,{"disambiguationData":[TD([[subQ2,-1.0]])],"derivedFrom":subQ1}),1.0]])]});}
            var Q80;
            {var subQ0=sQuery(id+"F9.wireOp",EDGE,"E65");var subQ1=sQuery(id+"F9.wireOp",EDGE,"E46.top");var subQ2=makeQuery(id+"F9.imprint","INTERSECT",VERTEX,{"disambiguationData":[OD(0.0)],"derivedFrom":[subQ1,subQ0]});Q80=makeQuery(id+"F9.imprint","IMPRINT",FACE,{"disambiguationData":[TD([[makeQuery(id+"F9.imprint","IMPRINT",EDGE,{"disambiguationData":[TD([[subQ2,-1.0]])],"derivedFrom":subQ1}),-1.0]])]});}
            var Q81;
            {var subQ0=sQuery(id+"F9.wireOp",EDGE,"E66");var subQ1=sQuery(id+"F9.wireOp",EDGE,"E46.top");var subQ2=makeQuery(id+"F9.imprint","INTERSECT",VERTEX,{"disambiguationData":[OD(0.0)],"derivedFrom":[subQ1,subQ0]});Q81=makeQuery(id+"F9.imprint","IMPRINT",FACE,{"disambiguationData":[TD([[makeQuery(id+"F9.imprint","IMPRINT",EDGE,{"disambiguationData":[TD([[subQ2,-1.0]])],"derivedFrom":subQ1}),1.0]])]});}
            var Q82;
            {var subQ0=sQuery(id+"F9.wireOp",EDGE,"E66");var subQ1=sQuery(id+"F9.wireOp",EDGE,"E46.top");var subQ2=makeQuery(id+"F9.imprint","INTERSECT",VERTEX,{"disambiguationData":[OD(0.0)],"derivedFrom":[subQ1,subQ0]});Q82=makeQuery(id+"F9.imprint","IMPRINT",FACE,{"disambiguationData":[TD([[makeQuery(id+"F9.imprint","IMPRINT",EDGE,{"disambiguationData":[TD([[subQ2,-1.0]])],"derivedFrom":subQ1}),-1.0]])]});}
            var Q83;
            {var subQ0=sQuery(id+"F9.wireOp",EDGE,"E67");var subQ1=sQuery(id+"F9.wireOp",EDGE,"E46.top");var subQ2=makeQuery(id+"F9.imprint","INTERSECT",VERTEX,{"disambiguationData":[OD(0.0)],"derivedFrom":[subQ1,subQ0]});Q83=makeQuery(id+"F9.imprint","IMPRINT",FACE,{"disambiguationData":[TD([[makeQuery(id+"F9.imprint","IMPRINT",EDGE,{"disambiguationData":[TD([[subQ2,-1.0]])],"derivedFrom":subQ1}),1.0]])]});}
            var Q84;
            {var subQ0=sQuery(id+"F9.wireOp",EDGE,"E67");var subQ1=sQuery(id+"F9.wireOp",EDGE,"E46.top");var subQ2=makeQuery(id+"F9.imprint","INTERSECT",VERTEX,{"disambiguationData":[OD(0.0)],"derivedFrom":[subQ1,subQ0]});Q84=makeQuery(id+"F9.imprint","IMPRINT",FACE,{"disambiguationData":[TD([[makeQuery(id+"F9.imprint","IMPRINT",EDGE,{"disambiguationData":[TD([[subQ2,-1.0]])],"derivedFrom":subQ1}),-1.0]])]});}
            var Q85;
            {var subQ0=sQuery(id+"F9.wireOp",EDGE,"E68");var subQ1=sQuery(id+"F9.wireOp",EDGE,"E61.top");var subQ2=makeQuery(id+"F9.imprint","INTERSECT",VERTEX,{"disambiguationData":[OD(0.0)],"derivedFrom":[subQ1,subQ0]});Q85=makeQuery(id+"F9.imprint","IMPRINT",FACE,{"disambiguationData":[TD([[makeQuery(id+"F9.imprint","IMPRINT",EDGE,{"disambiguationData":[TD([[subQ2,-1.0]])],"derivedFrom":subQ1}),1.0]])]});}
            var Q86;
            {var subQ0=sQuery(id+"F9.wireOp",EDGE,"E68");var subQ1=sQuery(id+"F9.wireOp",EDGE,"E61.top");var subQ2=makeQuery(id+"F9.imprint","INTERSECT",VERTEX,{"disambiguationData":[OD(0.0)],"derivedFrom":[subQ1,subQ0]});Q86=makeQuery(id+"F9.imprint","IMPRINT",FACE,{"disambiguationData":[TD([[makeQuery(id+"F9.imprint","IMPRINT",EDGE,{"disambiguationData":[TD([[subQ2,-1.0]])],"derivedFrom":subQ1}),-1.0]])]});}
            var Q87;
            {var subQ0=sQuery(id+"F9.wireOp",EDGE,"E69");var subQ1=sQuery(id+"F9.wireOp",EDGE,"E61.top");var subQ2=makeQuery(id+"F9.imprint","INTERSECT",VERTEX,{"disambiguationData":[OD(0.0)],"derivedFrom":[subQ1,subQ0]});Q87=makeQuery(id+"F9.imprint","IMPRINT",FACE,{"disambiguationData":[TD([[makeQuery(id+"F9.imprint","IMPRINT",EDGE,{"disambiguationData":[TD([[subQ2,-1.0]])],"derivedFrom":subQ1}),1.0]])]});}
            var Q88;
            {var subQ0=sQuery(id+"F9.wireOp",EDGE,"E69");var subQ1=sQuery(id+"F9.wireOp",EDGE,"E61.top");var subQ2=makeQuery(id+"F9.imprint","INTERSECT",VERTEX,{"disambiguationData":[OD(0.0)],"derivedFrom":[subQ1,subQ0]});Q88=makeQuery(id+"F9.imprint","IMPRINT",FACE,{"disambiguationData":[TD([[makeQuery(id+"F9.imprint","IMPRINT",EDGE,{"disambiguationData":[TD([[subQ2,-1.0]])],"derivedFrom":subQ1}),-1.0]])]});}
            var Q89;
            {var subQ0=sQuery(id+"F9.wireOp",EDGE,"E70");var subQ1=sQuery(id+"F9.wireOp",EDGE,"E61.top");var subQ2=makeQuery(id+"F9.imprint","INTERSECT",VERTEX,{"disambiguationData":[OD(0.0)],"derivedFrom":[subQ1,subQ0]});Q89=makeQuery(id+"F9.imprint","IMPRINT",FACE,{"disambiguationData":[TD([[makeQuery(id+"F9.imprint","IMPRINT",EDGE,{"disambiguationData":[TD([[subQ2,-1.0]])],"derivedFrom":subQ1}),1.0]])]});}
            var Q90;
            {var subQ0=sQuery(id+"F9.wireOp",EDGE,"E70");var subQ1=sQuery(id+"F9.wireOp",EDGE,"E61.top");var subQ2=makeQuery(id+"F9.imprint","INTERSECT",VERTEX,{"disambiguationData":[OD(0.0)],"derivedFrom":[subQ1,subQ0]});Q90=makeQuery(id+"F9.imprint","IMPRINT",FACE,{"disambiguationData":[TD([[makeQuery(id+"F9.imprint","IMPRINT",EDGE,{"disambiguationData":[TD([[subQ2,-1.0]])],"derivedFrom":subQ1}),-1.0]])]});}
            var Q91;
            {var subQ0=sQuery(id+"F9.wireOp",EDGE,"E71");var subQ1=sQuery(id+"F9.wireOp",EDGE,"E61.top");var subQ2=makeQuery(id+"F9.imprint","INTERSECT",VERTEX,{"disambiguationData":[OD(0.0)],"derivedFrom":[subQ1,subQ0]});Q91=makeQuery(id+"F9.imprint","IMPRINT",FACE,{"disambiguationData":[TD([[makeQuery(id+"F9.imprint","IMPRINT",EDGE,{"disambiguationData":[TD([[subQ2,-1.0]])],"derivedFrom":subQ1}),1.0]])]});}
            var Q92;
            {var subQ0=sQuery(id+"F9.wireOp",EDGE,"E71");var subQ1=sQuery(id+"F9.wireOp",EDGE,"E61.top");var subQ2=makeQuery(id+"F9.imprint","INTERSECT",VERTEX,{"disambiguationData":[OD(0.0)],"derivedFrom":[subQ1,subQ0]});Q92=makeQuery(id+"F9.imprint","IMPRINT",FACE,{"disambiguationData":[TD([[makeQuery(id+"F9.imprint","IMPRINT",EDGE,{"disambiguationData":[TD([[subQ2,-1.0]])],"derivedFrom":subQ1}),-1.0]])]});}
            var Q93;
            {var subQ0=sQuery(id+"F9.wireOp",EDGE,"E72");var subQ1=sQuery(id+"F9.wireOp",EDGE,"E61.top");var subQ2=makeQuery(id+"F9.imprint","INTERSECT",VERTEX,{"disambiguationData":[OD(0.0)],"derivedFrom":[subQ1,subQ0]});Q93=makeQuery(id+"F9.imprint","IMPRINT",FACE,{"disambiguationData":[TD([[makeQuery(id+"F9.imprint","IMPRINT",EDGE,{"disambiguationData":[TD([[subQ2,-1.0]])],"derivedFrom":subQ1}),1.0]])]});}
            var Q94;
            {var subQ0=sQuery(id+"F9.wireOp",EDGE,"E72");var subQ1=sQuery(id+"F9.wireOp",EDGE,"E61.top");var subQ2=makeQuery(id+"F9.imprint","INTERSECT",VERTEX,{"disambiguationData":[OD(0.0)],"derivedFrom":[subQ1,subQ0]});Q94=makeQuery(id+"F9.imprint","IMPRINT",FACE,{"disambiguationData":[TD([[makeQuery(id+"F9.imprint","IMPRINT",EDGE,{"disambiguationData":[TD([[subQ2,-1.0]])],"derivedFrom":subQ1}),-1.0]])]});}
            var Q95;
            {var subQ0=sQuery(id+"F9.wireOp",EDGE,"E73");var subQ1=sQuery(id+"F9.wireOp",EDGE,"E61.top");var subQ2=makeQuery(id+"F9.imprint","INTERSECT",VERTEX,{"disambiguationData":[OD(0.0)],"derivedFrom":[subQ1,subQ0]});Q95=makeQuery(id+"F9.imprint","IMPRINT",FACE,{"disambiguationData":[TD([[makeQuery(id+"F9.imprint","IMPRINT",EDGE,{"disambiguationData":[TD([[subQ2,-1.0]])],"derivedFrom":subQ1}),1.0]])]});}
            var Q96;
            {var subQ0=sQuery(id+"F9.wireOp",EDGE,"E73");var subQ1=sQuery(id+"F9.wireOp",EDGE,"E61.top");var subQ2=makeQuery(id+"F9.imprint","INTERSECT",VERTEX,{"disambiguationData":[OD(0.0)],"derivedFrom":[subQ1,subQ0]});Q96=makeQuery(id+"F9.imprint","IMPRINT",FACE,{"disambiguationData":[TD([[makeQuery(id+"F9.imprint","IMPRINT",EDGE,{"disambiguationData":[TD([[subQ2,-1.0]])],"derivedFrom":subQ1}),-1.0]])]});}
            extrude(context, id + "F10", {"entities" : qUnion([Q0, Q1, Q2, Q3, Q4, Q5, Q6, Q7, Q8, Q9, Q10, Q11, Q12, Q13, Q14, Q15, Q16, Q17, Q18, Q19, Q20, Q21, Q22, Q23, Q24, Q25, Q26, Q27, Q28, Q29, Q30, Q31, Q32, Q33, Q34, Q35, Q36, Q37, Q38, Q39, Q40, Q41, Q42, Q43, Q44, Q45, Q46, Q47, Q48, Q49, Q50, Q51, Q52, Q53, Q54, Q55, Q56, Q57, Q58, Q59, Q60, Q61, Q62, Q63, Q64, Q65, Q66, Q67, Q68, Q69, Q70, Q71, Q72, Q73, Q74, Q75, Q76, Q77, Q78, Q79, Q80, Q81, Q82, Q83, Q84, Q85, Q86, Q87, Q88, Q89, Q90, Q91, Q92, Q93, Q94, Q95, Q96]), "operationType" : NewBodyOperationType.REMOVE, "oppositeDirection" : true, "depth" : 25.98 * mm, "offsetDistance" : 25 * mm});
        }
        {
            var Q0;
            Q0=makeQuery(id+"F6.boolean.opBoolean","COPY",FACE,{"disambiguationData":[TD([makeQuery(id+"F1.opExtrude","SWEPT_FACE",FACE,{"disambiguationData":[OSD([sQuery(id+"F0.wireOp",EDGE,"E2.right")])]})])],"derivedFrom":makeQuery(id+"F6.opExtrude","SWEPT_FACE",FACE,{"disambiguationData":[OSD([sQuery(id+"F5.wireOp",EDGE,"E7.left")])]})});
            var sketch = newSketch(context, id + "F11", { "sketchPlane" : qUnion([Q0])});
            skLineSegment(sketch, "E74.bottom", {"start": v(-12.98, 2.6) * mm, "end": v(-10.07, 2.6) * mm});
            skLineSegment(sketch, "E74.top", {"start": v(-12.98, 0) * mm, "end": v(-10.07, 0) * mm});
            skLineSegment(sketch, "E74.left", {"start": v(-12.98, 2.6) * mm, "end": v(-12.98, 0) * mm});
            skLineSegment(sketch, "E74.right", {"start": v(-10.07, 2.6) * mm, "end": v(-10.07, 0) * mm});
            skLineSegment(sketch, "E75.bottom", {"start": v(-10.07, 2.6) * mm, "end": v(-5.32, 2.6) * mm});
            skLineSegment(sketch, "E75.top", {"start": v(-10.07, 0) * mm, "end": v(-5.32, 0) * mm});
            skLineSegment(sketch, "E75.right", {"start": v(-5.32, 2.6) * mm, "end": v(-5.32, 0) * mm});
            skSolve(sketch);
        }
        {
            var Q0;
            Q0=makeQuery(id+"F11.imprint","IMPRINT",FACE,{"disambiguationData":[TD([[makeQuery(id+"F11.imprint","IMPRINT",EDGE,{"derivedFrom":sQuery(id+"F11.wireOp",EDGE,"E75.bottom")}),1.0]])]});
            extrude(context, id + "F12", {"entities" : qUnion([Q0]), "operationType" : NewBodyOperationType.REMOVE, "oppositeDirection" : true, "depth" : 6 * mm, "offsetDistance" : 25 * mm});
        }
        {
            var Q0;
            Q0=makeQuery(id+"F6.boolean.opBoolean","COPY",FACE,{"disambiguationData":[TD([makeQuery(id+"F1.opExtrude","SWEPT_FACE",FACE,{"disambiguationData":[OSD([sQuery(id+"F0.wireOp",EDGE,"E1.right")])]})])],"derivedFrom":makeQuery(id+"F6.opExtrude","SWEPT_FACE",FACE,{"disambiguationData":[OSD([sQuery(id+"F5.wireOp",EDGE,"E7.left")])]})});
            var sketch = newSketch(context, id + "F13", { "sketchPlane" : qUnion([Q0])});
            skLineSegment(sketch, "E76.bottom", {"start": v(12.98, 2.6) * mm, "end": v(10.07, 2.6) * mm});
            skLineSegment(sketch, "E76.top", {"start": v(12.98, 0) * mm, "end": v(10.07, 0) * mm});
            skLineSegment(sketch, "E76.left", {"start": v(12.98, 2.6) * mm, "end": v(12.98, 0) * mm});
            skLineSegment(sketch, "E76.right", {"start": v(10.07, 2.6) * mm, "end": v(10.07, 0) * mm});
            skLineSegment(sketch, "E77.bottom", {"start": v(5.32, 0) * mm, "end": v(10.07, 0) * mm});
            skLineSegment(sketch, "E77.top", {"start": v(5.32, 2.6) * mm, "end": v(10.07, 2.6) * mm});
            skLineSegment(sketch, "E77.left", {"start": v(5.32, 0) * mm, "end": v(5.32, 2.6) * mm});
            skLineSegment(sketch, "E77.right", {"start": v(10.07, 0) * mm, "end": v(10.07, 2.6) * mm});
            skSolve(sketch);
        }
        {
            var Q0;
            Q0=makeQuery(id+"F13.imprint","IMPRINT",FACE,{"disambiguationData":[TD([[makeQuery(id+"F13.imprint","IMPRINT",EDGE,{"derivedFrom":sQuery(id+"F13.wireOp",EDGE,"E77.bottom")}),-1.0]])]});
            extrude(context, id + "F14", {"entities" : qUnion([Q0]), "operationType" : NewBodyOperationType.REMOVE, "oppositeDirection" : true, "depth" : 6 * mm, "offsetDistance" : 25 * mm});
        }
        {
            var Q0;
            {var subQ3=sQuery(id+"F0.wireOp",EDGE,"E0.bottom");Q0=makeQuery(id+"F4.boolean.opBoolean","SPLIT",FACE,{"disambiguationData":[TD([makeQuery(id+"F1.opExtrude","SWEPT_FACE",FACE,{"disambiguationData":[OSD([sQuery(id+"F0.wireOp",EDGE,"E1.top")])]})])],"derivedFrom":makeQuery(id+"F2.opExtrude","CAP_FACE",FACE,{"disambiguationData":[OSD([subQ3,sQuery(id+"F0.wireOp",EDGE,"E0.top"),sQuery(id+"F0.wireOp",EDGE,"E1.left"),sQuery(id+"F0.wireOp",EDGE,"E2.left")])],"isStart":false})});}
            var sketch = newSketch(context, id + "F15", { "sketchPlane" : qUnion([Q0])});
            skSolve(sketch);
        }
        {
            var Q0;
            {var subQ0=sQuery(id+"F0.wireOp",EDGE,"E0.bottom");Q0=makeQuery(id+"F15.imprint","IMPRINT",FACE,{"disambiguationData":[TD([[makeQuery(id+"F15.imprint","IMPRINT",EDGE,{"derivedFrom":makeQuery(id+"F2.opExtrude","CAP_EDGE",EDGE,{"disambiguationData":[OSD([subQ0])],"isStart":false})}),-1.0]])]});}
            extrude(context, id + "F16", {"entities" : qUnion([Q0]), "operationType" : NewBodyOperationType.REMOVE, "oppositeDirection" : true, "depth" : 2.4 * mm, "offsetDistance" : 25 * mm});
        }
    });
